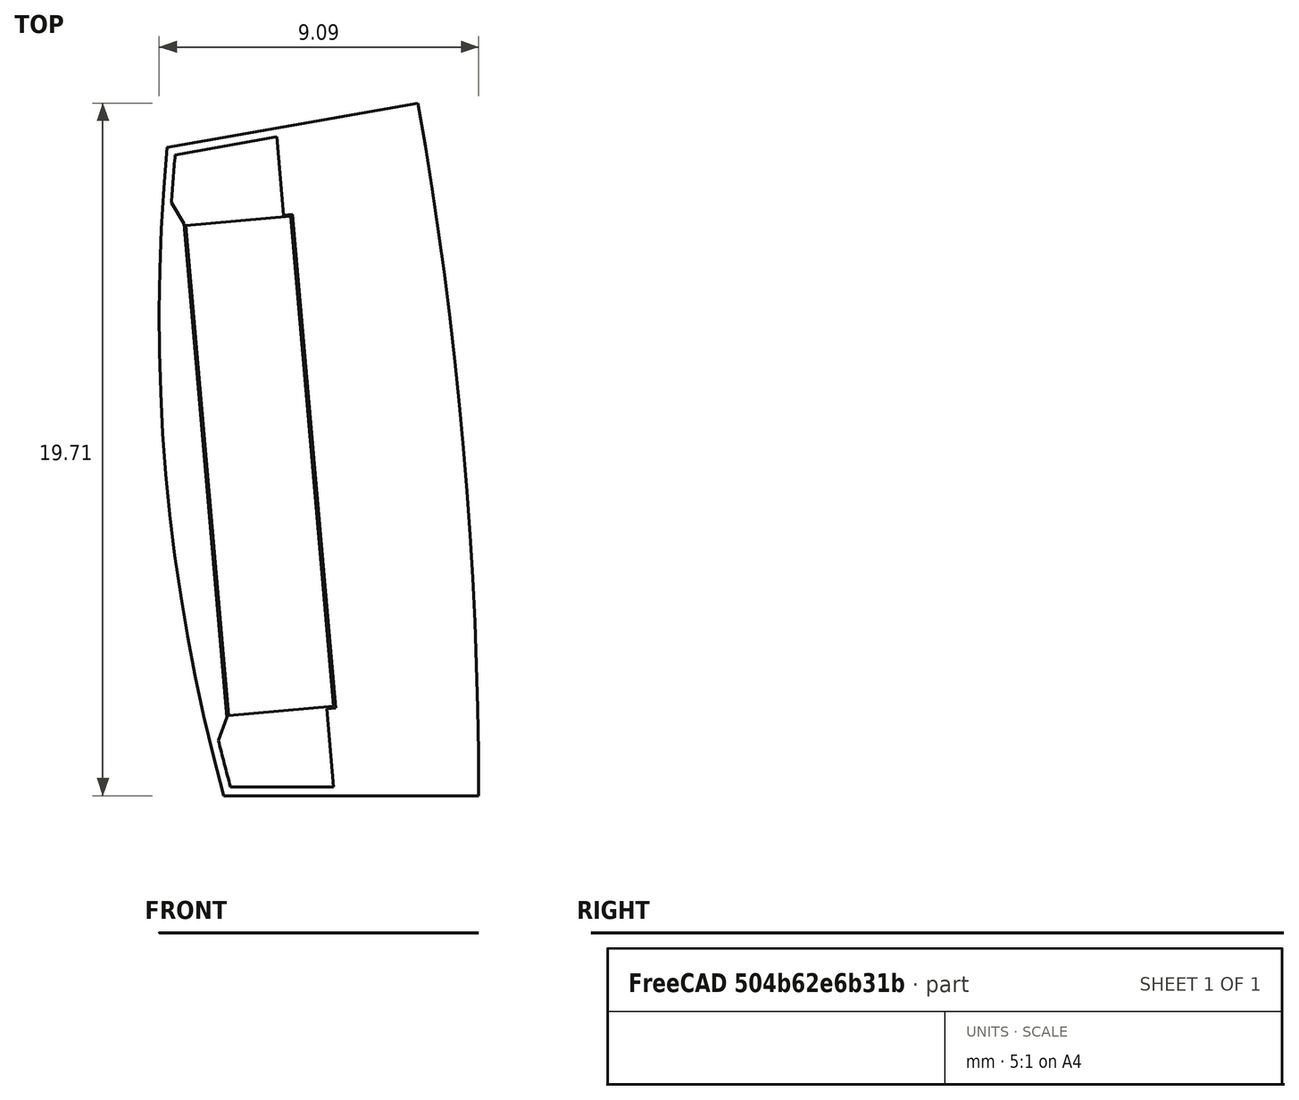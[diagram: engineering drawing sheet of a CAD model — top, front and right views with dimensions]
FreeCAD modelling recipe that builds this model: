
FCSTD DOCUMENT  (FreeCAD 0.18R4 (GitTag))
Label: RotorORBlockPocket
License: All rights reserved
LicenseURL: http://en.wikipedia.org/wiki/All_rights_reserved
objects: Sketcher::SketchObject×6, Surface::Filling×3, PartDesign::Body×2, Spreadsheet::Sheet×1, Part::Cut×1
note: 12 computed .brp shape members not serialized (recipe doc carries the construction recipe); baked Part::Feature solids carry a one-line shape summary decoded from their .brp

FEATURE [Spreadsheet::Sheet] Spreadsheet  label="Variables"
  cells = A2=poleNumber; B2(poleNumber)=36; C2=ok; A3=outerDiameter; B3(outerDiameter)=227; C3=ok; D3=Calc Value; A4=innerDiameter; B4(innerDiameter)=210; C4=ok; D4=Input Value; A5=stackLength; B5(stackLength)=20; C5=ok; D5=UsedParameter; A6=stackingFactor; B6(stackingFactor)=0.95; A7=embrace; B7(embrace)=80; A8=contourRatio; B8(contourRatio)=90; A9=magnetAirgap; B9(magnetAirgap)=0.05; C9=ok; A10=poleSeparation; B10(poleSeparation)=2; A11=magnetWidth; B11(magnetWidth)=14; C11=ok; A12=magnetHeight; B12(magnetHeight)=3; C12=ok; A13=rib; B13(rib)=0.5; C13=ok; A14=bridgeCurved; B14(bridgeCurved)=0.25; C14=ok; A15=cutTop; B15(cutTop)=0.2; A16=cutBottom; B16(cutBottom)=0.25; C16=ok; A17=segmentAngle; B17(segmentAngle)==360 / poleNumber; A18=movePocketInwards; B18(movePocketInwards)=0.3; C18=ok; A19=cuttingThickness; B19(cuttingThickness)=0.01; A20=magnetLength; B20(magnetLength)=20; A21=cut; B21(cut)=0.2; A22=ribShaft; B22(ribShaft)=0.5; A23=magnetEmbrace; B23(magnetEmbrace)=70; A24=magnetContourRatio; B24(magnetContourRatio)=95; A25=axialMisalignment; B25(axialMisalignment)=0.5; C25=ok; A26=magnetContactRatio; B26(magnetContactRatio)=83; C26=ok
FEATURE [Sketcher::SketchObject] Sketch003  label="RotorSketch"
  MapMode = 5
  Support = -> [XY_Plane]
  expr: Constraints[84] = Variables.magnetHeight + Variables.magnetAirgap * 2
  expr: Constraints[80] = Variables.movePocketInwards
  expr: Constraints[14] = Variables.innerDiameter / 2
  expr: Constraints[81] = Variables.magnetWidth + Variables.magnetAirgap * 2
  expr: Constraints[28] = Variables.segmentAngle * Variables.magnetContactRatio / 100
  expr: Constraints[48] = Variables.rib / 2
  expr: Constraints[86] = Variables.magnetHeight + Variables.magnetAirgap * 2 - Variables.cutBottom
  expr: Constraints[37] = Variables.bridgeCurved
  expr: Constraints[33] = (Variables.outerDiameter - Variables.innerDiameter) / 2 * (1 - Variables.contourRatio / 100)
  expr: Constraints[15] = Variables.outerDiameter / 2
  expr: Constraints[18] = Variables.segmentAngle / 2
  expr: Constraints[0] = Variables.segmentAngle
  expr: Constraints[40] = Variables.bridgeCurved
  sketch-geometry (38):
    g0: LineSegment [constr] StartX=105 StartY=0 StartZ=0 EndX=113.5 EndY=0 EndZ=0
    g1: LineSegment [constr] StartX=103.405 StartY=18.2331 StartZ=0 EndX=111.776 EndY=19.7091 EndZ=0
    g2: LineSegment [constr] StartX=0 StartY=0 StartZ=0 EndX=105 EndY=0 EndZ=0
    g3: LineSegment [constr] StartX=0 StartY=0 StartZ=0 EndX=103.405 EndY=18.2331 EndZ=0
    g4: ArcOfCircle CenterX=0 CenterY=0 CenterZ=0 NormalX=0 NormalY=0 NormalZ=1 AngleXU=0 Radius=113.5 StartAngle=0 EndAngle=0.174533
    g5: ArcOfCircle [constr] CenterX=0 CenterY=0 CenterZ=0 NormalX=0 NormalY=0 NormalZ=1 AngleXU=0 Radius=105 StartAngle=0 EndAngle=0.174533
    g6: LineSegment [constr] StartX=0 StartY=0 StartZ=0 EndX=113.068 EndY=9.89218 EndZ=0
    g7: LineSegment [constr] StartX=103.8 StartY=18.3027 StartZ=0 EndX=105.401 EndY=0 EndZ=0
    g8: LineSegment [constr] StartX=104.759 StartY=16.8734 StartZ=0 EndX=106.097 EndY=1.5741 EndZ=0
    g9: LineSegment [constr] StartX=0 StartY=0 StartZ=0 EndX=104.759 EndY=16.8734 EndZ=0
    g10: LineSegment [constr] StartX=0 StartY=0 StartZ=0 EndX=106.097 EndY=1.5741 EndZ=0
    g11: ArcOfCircle CenterX=155.466 CenterY=13.6015 CenterZ=0 NormalX=0 NormalY=0 NormalZ=1 AngleXU=0 Radius=51.0601 StartAngle=3.04649 EndAngle=3.41123
    g12: ArcOfCircle [constr] CenterX=155.715 CenterY=13.6233 CenterZ=0 NormalX=0 NormalY=0 NormalZ=1 AngleXU=0 Radius=51.0601 StartAngle=3.04604 EndAngle=3.41167
    g13: LineSegment [constr] StartX=104.6 StartY=9.15135 StartZ=0 EndX=104.849 EndY=9.17314 EndZ=0
    g14: LineSegment [constr] StartX=104.864 StartY=18.2365 StartZ=0 EndX=111.819 EndY=19.4628 EndZ=0
    g15: LineSegment [constr] StartX=111.819 StartY=19.4628 StartZ=0 EndX=111.775 EndY=19.709 EndZ=0
    g16: LineSegment [constr] StartX=113.5 StartY=0.25 StartZ=0 EndX=106.438 EndY=0.25 EndZ=0
    g17: LineSegment [constr] StartX=113.5 StartY=0.25 StartZ=0 EndX=113.5 EndY=0 EndZ=0
    g18: LineSegment [constr] StartX=104.864 StartY=18.2365 StartZ=0 EndX=106.438 EndY=0.25 EndZ=0
    g19: LineSegment StartX=104.637 StartY=18.4503 StartZ=0 EndX=111.776 EndY=19.7091 EndZ=0
    g20: LineSegment [constr] StartX=106.251 StartY=0 StartZ=0 EndX=113.5 EndY=0 EndZ=0
    g21: ArcOfCircle [constr] CenterX=155.715 CenterY=13.6233 CenterZ=0 NormalX=0 NormalY=0 NormalZ=1 AngleXU=0 Radius=51.0601 StartAngle=3.05112 EndAngle=3.0779
    g22: ArcOfCircle [constr] CenterX=155.715 CenterY=13.6233 CenterZ=0 NormalX=0 NormalY=0 NormalZ=1 AngleXU=0 Radius=51.0601 StartAngle=3.37982 EndAngle=3.4066
    g23: LineSegment [constr] StartX=104.759 StartY=16.8734 StartZ=0 EndX=104.508 EndY=18.4276 EndZ=0
    g24: LineSegment [constr] StartX=104.759 StartY=16.8734 StartZ=0 EndX=105.112 EndY=16.2731 EndZ=0
    g25: LineSegment [constr] StartX=105.112 StartY=16.2731 StartZ=0 EndX=106.341 EndY=2.22673 EndZ=0
    g26: LineSegment [constr] StartX=106.097 StartY=1.5741 StartZ=0 EndX=106.341 EndY=2.22673 EndZ=0
    g27: LineSegment [constr] StartX=104.759 StartY=16.8734 StartZ=0 EndX=105.058 EndY=16.8996 EndZ=0
    g28: LineSegment [constr] StartX=105.112 StartY=16.2731 StartZ=0 EndX=108.201 EndY=16.5433 EndZ=0
    g29: LineSegment [constr] StartX=105.112 StartY=16.2731 StartZ=0 EndX=107.952 EndY=16.5215 EndZ=0
    g30: LineSegment [constr] StartX=107.952 StartY=16.5215 StartZ=0 EndX=107.757 EndY=18.7466 EndZ=0
    g31: LineSegment [constr] StartX=107.952 StartY=16.5215 StartZ=0 EndX=108.201 EndY=16.5433 EndZ=0
    g32: LineSegment [constr] StartX=104.864 StartY=18.2365 StartZ=0 EndX=107.757 EndY=18.7466 EndZ=0
    g33: LineSegment [constr] StartX=109.43 StartY=2.49691 StartZ=0 EndX=109.18 EndY=2.47512 EndZ=0
    g34: LineSegment [constr] StartX=109.18 StartY=2.47512 StartZ=0 EndX=109.375 EndY=0.25 EndZ=0
    g35: LineSegment [constr] StartX=106.438 StartY=0.25 StartZ=0 EndX=109.375 EndY=0.25 EndZ=0
    g36: LineSegment [constr] StartX=109.43 StartY=2.49691 StartZ=0 EndX=108.201 EndY=16.5433 EndZ=0
    g37: LineSegment StartX=106.251 StartY=0 StartZ=0 EndX=113.5 EndY=0 EndZ=0
  constraints (105):
    c: Angle(g0,g1) = 0.174533
    c: Coincident(g2,g-1)
    c: Coincident(g2,g0)
    c: Coincident(g3,g2)
    c: Coincident(g3,g1)
    c: Parallel(g2,g0)
    c: Parallel(g3,g1)
    c: Coincident(g4,g-1)
    c: Coincident(g4,g0)
    c: Coincident(g4,g1)
    c: Coincident(g5,g4)
    c: Coincident(g5,g1)
    c: Coincident(g5,g0)
    c: Angle(g-1,g2) = 0
    c: Radius(g5) = 105
    c: Radius(g4) = 113.5
    c: Coincident(g6,g5)
    c: PointOnObject(g6,g4)
    c: Angle(g-1,g6) = 0.0872665
    c: PointOnObject(g7,g0)
    c: Tangent(g7,g5)
    c: Angle(g6,g7) = 1.5708
    c: PointOnObject(g7,g1)
    c: Symmetric(g8,g8,g6)
    c: Coincident(g9,g5)
    c: Coincident(g9,g8)
    c: Coincident(g10,g5)
    c: Coincident(g10,g8)
    c: Angle(g10,g9) = 0.144862
    c: PointOnObject(g11,g6)
    c: PointOnObject(g11,g1)
    c: PointOnObject(g11,g0)
    c: Tangent(g11,g7)
    c: Distance(g7,g11) = 0.85
    c: PointOnObject(g12,g6)
    c: PointOnObject(g12,g1)
    c: PointOnObject(g12,g0)
    c: Distance(g11,g12) = 0.25
    c: PointOnObject(g13,g11)
    c: PointOnObject(g13,g12)
    c: Distance(g13) = 0.25
    c: Parallel(g13,g6)
    c: PointOnObject(g13,g6)
    c: PointOnObject(g14,g12)
    c: PointOnObject(g14,g4)
    c: Coincident(g15,g14)
    c: PointOnObject(g15,g1)
    c: Angle(g15,g14) = 1.5708
    c: Distance(g15) = 0.25
    c: Angle(g1,g15) = 1.5708
    c: PointOnObject(g16,g4)
    c: Coincident(g17,g16)
    c: PointOnObject(g17,g0)
    c: Angle(g16,g17) = 1.5708
    c: Angle(g17,g0) = 1.5708
    c: Equal(g17,g15)
    c: Coincident(g18,g14)
    c: Coincident(g18,g16)
    c: Coincident(g19,g11)
    c: Coincident(g19,g1)
    c: Coincident(g20,g11)
    c: Coincident(g20,g17)
    c: Coincident(g21,g12)
    c: Coincident(g21,g8)
    c: Coincident(g21,g14)
    c: Coincident(g22,g21)
    c: Coincident(g22,g16)
    c: Coincident(g22,g8)
    c: Coincident(g23,g21)
    c: PointOnObject(g23,g1)
    c: Angle(g23,g9) = 1.5708
    c: Coincident(g24,g21)
    c: Coincident(g25,g24)
    c: Coincident(g26,g22)
    c: Coincident(g26,g25)
    c: Equal(g26,g24)
    c: Symmetric(g24,g25,g6)
    c: Coincident(g27,g21)
    c: PointOnObject(g27,g25)
    c: Angle(g27,g25) = 1.5708
    c: Distance(g27) = 0.3
    c: Distance(g25) = 14.1
    c: Coincident(g28,g24)
    c: Angle(g25,g28) = 1.5708
    c: Distance(g28) = 3.1
    c: Coincident(g29,g24)
    c: Distance(g29) = 2.85
    c: Angle(g25,g29) = 1.5708
    c: Coincident(g30,g29)
    c: PointOnObject(g30,g14)
    c: Coincident(g31,g30)
    c: Coincident(g31,g28)
    c: Coincident(g32,g21)
    c: Coincident(g32,g30)
    c: Parallel(g18,g30)
    c: Coincident(g34,g33)
    c: Symmetric(g31,g33,g6)
    c: Symmetric(g30,g33,g6)
    c: Symmetric(g30,g34,g6)
    c: Coincident(g35,g22)
    c: Coincident(g35,g34)
    c: Coincident(g36,g33)
    c: Coincident(g36,g31)
    c: Coincident(g37,g11)
    c: Coincident(g37,g4)
FEATURE [Sketcher::SketchObject] Sketch004  label="BoundingBox"
  MapMode = 5
  Support = -> [XY_Plane]
  expr: Constraints[8] = Variables.outerDiameter
  sketch-geometry (6):
    g0: LineSegment StartX=-113.5 StartY=-113.5 StartZ=0 EndX=113.5 EndY=-113.5 EndZ=0
    g1: LineSegment StartX=113.5 StartY=-113.5 StartZ=0 EndX=113.5 EndY=113.5 EndZ=0
    g2: LineSegment StartX=113.5 StartY=113.5 StartZ=0 EndX=-113.5 EndY=113.5 EndZ=0
    g3: LineSegment StartX=-113.5 StartY=113.5 StartZ=0 EndX=-113.5 EndY=-113.5 EndZ=0
    g4: LineSegment [constr] StartX=-113.5 StartY=-113.5 StartZ=0 EndX=113.5 EndY=113.5 EndZ=0
    g5: GeomPoint X=4.4e-15 Y=-1.8e-15 Z=0
  constraints (14):
    c: Coincident(g0,g1)
    c: Coincident(g1,g2)
    c: Coincident(g2,g3)
    c: Coincident(g3,g0)
    c: Horizontal(g0)
    c: Horizontal(g2)
    c: Vertical(g1)
    c: Vertical(g3)
    c: DistanceY(g1,g1) = 227
    c: Equal(g2,g1)
    c: Coincident(g4,g0)
    c: Coincident(g4,g1)
    c: Symmetric(g0,g1,g5)
    c: Coincident(g-1,g5)
FEATURE [Sketcher::SketchObject] Sketch005  label="RotorSideSketch"
  MapMode = 5
  Support = -> [XY_Plane001]
  expr: Constraints[22] = Variables.stackLength / 2 - Variables.axialMisalignment
  expr: Constraints[9] = Variables.outerDiameter / 2
  expr: Constraints[8] = Variables.innerDiameter / 2
  expr: Constraints[7] = Variables.stackLength
  sketch-geometry (8):
    g0: LineSegment StartX=-9.5 StartY=105 StartZ=0 EndX=10.5 EndY=105 EndZ=0
    g1: LineSegment StartX=10.5 StartY=105 StartZ=0 EndX=10.5 EndY=113.5 EndZ=0
    g2: LineSegment StartX=10.5 StartY=113.5 StartZ=0 EndX=-9.5 EndY=113.5 EndZ=0
    g3: LineSegment StartX=-9.5 StartY=113.5 StartZ=0 EndX=-9.5 EndY=105 EndZ=0
    g4: LineSegment StartX=-9.5 StartY=-105 StartZ=0 EndX=10.5 EndY=-105 EndZ=0
    g5: LineSegment StartX=10.5 StartY=-105 StartZ=0 EndX=10.5 EndY=-113.5 EndZ=0
    g6: LineSegment StartX=10.5 StartY=-113.5 StartZ=0 EndX=-9.5 EndY=-113.5 EndZ=0
    g7: LineSegment StartX=-9.5 StartY=-113.5 StartZ=0 EndX=-9.5 EndY=-105 EndZ=0
  constraints (23):
    c: Coincident(g0,g1)
    c: Coincident(g1,g2)
    c: Coincident(g2,g3)
    c: Coincident(g3,g0)
    c: Horizontal(g0)
    c: Vertical(g1)
    c: Vertical(g3)
    c: DistanceX(g2,g2) = 20
    c: DistanceY(g-1,g0) = 105
    c: DistanceY(g-1,g1) = 113.5
    c: Coincident(g4,g5)
    c: Coincident(g5,g6)
    c: Coincident(g6,g7)
    c: Coincident(g7,g4)
    c: Horizontal(g4)
    c: Vertical(g5)
    c: Vertical(g7)
    c: Equal(g4,g0)
    c: Equal(g7,g3)
    c: Horizontal(g2)
    c: Horizontal(g6)
    c: Symmetric(g4,g0,g-1)
    c: DistanceX(g0,g-1) = 9.5
FEATURE [Sketcher::SketchObject] Sketch006  label="MagnetSideSketch"
  MapMode = 5
  Support = -> [XY_Plane001]
  expr: Constraints[20] = Variables.stackLength / 2 - Variables.axialMisalignment
  expr: Constraints[17] = Variables.innerDiameter / 2
  expr: Constraints[14] = Variables.stackLength
  expr: Constraints[3] = Variables.magnetHeight
  sketch-geometry (8):
    g0: LineSegment StartX=-9.5 StartY=105 StartZ=0 EndX=10.5 EndY=105 EndZ=0
    g1: LineSegment StartX=10.5 StartY=105 StartZ=0 EndX=10.5 EndY=108 EndZ=0
    g2: LineSegment StartX=-9.5 StartY=108 StartZ=0 EndX=-9.5 EndY=105 EndZ=0
    g3: LineSegment StartX=-9.5 StartY=-105 StartZ=0 EndX=10.5 EndY=-105 EndZ=0
    g4: LineSegment StartX=10.5 StartY=-105 StartZ=0 EndX=10.5 EndY=-108 EndZ=0
    g5: LineSegment StartX=10.5 StartY=-108 StartZ=0 EndX=-9.5 EndY=-108 EndZ=0
    g6: LineSegment StartX=-9.5 StartY=-108 StartZ=0 EndX=-9.5 EndY=-105 EndZ=0
    g7: LineSegment StartX=-9.5 StartY=108 StartZ=0 EndX=10.5 EndY=108 EndZ=0
  constraints (23):
    c: Coincident(g0,g1)
    c: Coincident(g2,g0)
    c: Horizontal(g0)
    c: DistanceY(g1,g1) = 3
    c: Coincident(g3,g4)
    c: Coincident(g4,g5)
    c: Coincident(g5,g6)
    c: Coincident(g6,g3)
    c: Horizontal(g3)
    c: Vertical(g4)
    c: Vertical(g6)
    c: Equal(g6,g2)
    c: Coincident(g7,g2)
    c: Coincident(g7,g1)
    c: DistanceX(g7,g7) = 20
    c: Horizontal(g5)
    c: Equal(g6,g1)
    c: DistanceY(g-1,g0) = 105
    c: Symmetric(g0,g3,g-1)
    c: Equal(g5,g7)
    c: DistanceX(g0,g-1) = 9.5
    c: Angle(g0,g2) = 1.5708
    c: Angle(g1,g0) = 1.5708
FEATURE [PartDesign::Body] Body001  label="SideView"
  Group = -> [Sketch005,Sketch006]
  Origin = -> Origin001
FEATURE [Surface::Filling] Surface001  label="Pole_Surface"
  Anisotropy = false
  BoundaryEdges = -> [Sketch003]
  BoundaryOrder = [0,0,0,0]
  Degree = 3
  Iterations = 2
  MaximumDegree = 8
  MaximumSegments = 9
  PointsOnCurve = 15
  TolAngular = 0.01
  TolCurvature = 0.1
  Tolerance2d = 1e-05
  Tolerance3d = 0.0001
FEATURE [Sketcher::SketchObject] Sketch007  label="PocketSketch"
  MapMode = 5
  Support = -> [XY_Plane]
  expr: Constraints[84] = Variables.magnetHeight + Variables.magnetAirgap * 2
  expr: Constraints[80] = Variables.movePocketInwards
  expr: Constraints[14] = Variables.innerDiameter / 2
  expr: Constraints[81] = Variables.magnetWidth + Variables.magnetAirgap * 2
  expr: Constraints[28] = Variables.segmentAngle * Variables.magnetContactRatio / 100
  expr: Constraints[48] = Variables.rib / 2
  expr: Constraints[86] = Variables.magnetHeight + Variables.magnetAirgap * 2 - Variables.cutBottom
  expr: Constraints[37] = Variables.bridgeCurved
  expr: Constraints[33] = (Variables.outerDiameter - Variables.innerDiameter) / 2 * (1 - Variables.contourRatio / 100)
  expr: Constraints[15] = Variables.outerDiameter / 2
  expr: Constraints[18] = Variables.segmentAngle / 2
  expr: Constraints[0] = Variables.segmentAngle
  expr: Constraints[40] = Variables.bridgeCurved
  sketch-geometry (38):
    g0: LineSegment [constr] StartX=105 StartY=0 StartZ=0 EndX=113.5 EndY=0 EndZ=0
    g1: LineSegment [constr] StartX=103.405 StartY=18.2331 StartZ=0 EndX=111.776 EndY=19.7091 EndZ=0
    g2: LineSegment [constr] StartX=0 StartY=0 StartZ=0 EndX=105 EndY=0 EndZ=0
    g3: LineSegment [constr] StartX=0 StartY=0 StartZ=0 EndX=103.405 EndY=18.2331 EndZ=0
    g4: ArcOfCircle [constr] CenterX=0 CenterY=0 CenterZ=0 NormalX=0 NormalY=0 NormalZ=1 AngleXU=0 Radius=113.5 StartAngle=0 EndAngle=0.174533
    g5: ArcOfCircle [constr] CenterX=0 CenterY=0 CenterZ=0 NormalX=0 NormalY=0 NormalZ=1 AngleXU=0 Radius=105 StartAngle=0 EndAngle=0.174533
    g6: LineSegment [constr] StartX=0 StartY=0 StartZ=0 EndX=113.068 EndY=9.89218 EndZ=0
    g7: LineSegment [constr] StartX=103.8 StartY=18.3027 StartZ=0 EndX=105.401 EndY=0 EndZ=0
    g8: LineSegment [constr] StartX=104.759 StartY=16.8734 StartZ=0 EndX=106.097 EndY=1.5741 EndZ=0
    g9: LineSegment [constr] StartX=0 StartY=0 StartZ=0 EndX=104.759 EndY=16.8734 EndZ=0
    g10: LineSegment [constr] StartX=0 StartY=0 StartZ=0 EndX=106.097 EndY=1.5741 EndZ=0
    g11: ArcOfCircle [constr] CenterX=155.466 CenterY=13.6015 CenterZ=0 NormalX=0 NormalY=0 NormalZ=1 AngleXU=0 Radius=51.0601 StartAngle=3.04649 EndAngle=3.41123
    g12: ArcOfCircle [constr] CenterX=155.715 CenterY=13.6233 CenterZ=0 NormalX=0 NormalY=0 NormalZ=1 AngleXU=0 Radius=51.0601 StartAngle=3.04604 EndAngle=3.41167
    g13: LineSegment [constr] StartX=104.6 StartY=9.15135 StartZ=0 EndX=104.849 EndY=9.17314 EndZ=0
    g14: LineSegment [constr] StartX=104.864 StartY=18.2365 StartZ=0 EndX=111.819 EndY=19.4628 EndZ=0
    g15: LineSegment [constr] StartX=111.819 StartY=19.4628 StartZ=0 EndX=111.775 EndY=19.709 EndZ=0
    g16: LineSegment [constr] StartX=113.5 StartY=0.25 StartZ=0 EndX=106.438 EndY=0.25 EndZ=0
    g17: LineSegment [constr] StartX=113.5 StartY=0.25 StartZ=0 EndX=113.5 EndY=0 EndZ=0
    g18: LineSegment [constr] StartX=104.864 StartY=18.2365 StartZ=0 EndX=106.438 EndY=0.25 EndZ=0
    g19: LineSegment [constr] StartX=104.637 StartY=18.4503 StartZ=0 EndX=111.776 EndY=19.7091 EndZ=0
    g20: LineSegment [constr] StartX=106.251 StartY=0 StartZ=0 EndX=113.5 EndY=0 EndZ=0
    g21: ArcOfCircle CenterX=155.715 CenterY=13.6233 CenterZ=0 NormalX=0 NormalY=0 NormalZ=1 AngleXU=0 Radius=51.0601 StartAngle=3.05112 EndAngle=3.0779
    g22: ArcOfCircle CenterX=155.715 CenterY=13.6233 CenterZ=0 NormalX=0 NormalY=0 NormalZ=1 AngleXU=0 Radius=51.0601 StartAngle=3.37982 EndAngle=3.4066
    g23: LineSegment [constr] StartX=104.759 StartY=16.8734 StartZ=0 EndX=104.508 EndY=18.4276 EndZ=0
    g24: LineSegment StartX=104.759 StartY=16.8734 StartZ=0 EndX=105.112 EndY=16.2731 EndZ=0
    g25: LineSegment StartX=105.112 StartY=16.2731 StartZ=0 EndX=106.341 EndY=2.22673 EndZ=0
    g26: LineSegment StartX=106.097 StartY=1.5741 StartZ=0 EndX=106.341 EndY=2.22673 EndZ=0
    g27: LineSegment [constr] StartX=104.759 StartY=16.8734 StartZ=0 EndX=105.058 EndY=16.8996 EndZ=0
    g28: LineSegment [constr] StartX=105.112 StartY=16.2731 StartZ=0 EndX=108.201 EndY=16.5433 EndZ=0
    g29: LineSegment [constr] StartX=105.112 StartY=16.2731 StartZ=0 EndX=107.952 EndY=16.5215 EndZ=0
    g30: LineSegment StartX=107.952 StartY=16.5215 StartZ=0 EndX=107.757 EndY=18.7466 EndZ=0
    g31: LineSegment StartX=107.952 StartY=16.5215 StartZ=0 EndX=108.201 EndY=16.5433 EndZ=0
    g32: LineSegment StartX=104.864 StartY=18.2365 StartZ=0 EndX=107.757 EndY=18.7466 EndZ=0
    g33: LineSegment StartX=109.43 StartY=2.49691 StartZ=0 EndX=109.18 EndY=2.47512 EndZ=0
    g34: LineSegment StartX=109.18 StartY=2.47512 StartZ=0 EndX=109.375 EndY=0.25 EndZ=0
    g35: LineSegment StartX=106.438 StartY=0.25 StartZ=0 EndX=109.375 EndY=0.25 EndZ=0
    g36: LineSegment StartX=109.43 StartY=2.49691 StartZ=0 EndX=108.201 EndY=16.5433 EndZ=0
    g37: LineSegment [constr] StartX=106.251 StartY=0 StartZ=0 EndX=113.5 EndY=0 EndZ=0
  constraints (105):
    c: Angle(g0,g1) = 0.174533
    c: Coincident(g2,g-1)
    c: Coincident(g2,g0)
    c: Coincident(g3,g2)
    c: Coincident(g3,g1)
    c: Parallel(g2,g0)
    c: Parallel(g3,g1)
    c: Coincident(g4,g-1)
    c: Coincident(g4,g0)
    c: Coincident(g4,g1)
    c: Coincident(g5,g4)
    c: Coincident(g5,g1)
    c: Coincident(g5,g0)
    c: Angle(g-1,g2) = 0
    c: Radius(g5) = 105
    c: Radius(g4) = 113.5
    c: Coincident(g6,g5)
    c: PointOnObject(g6,g4)
    c: Angle(g-1,g6) = 0.0872665
    c: PointOnObject(g7,g0)
    c: Tangent(g7,g5)
    c: Angle(g6,g7) = 1.5708
    c: PointOnObject(g7,g1)
    c: Symmetric(g8,g8,g6)
    c: Coincident(g9,g5)
    c: Coincident(g9,g8)
    c: Coincident(g10,g5)
    c: Coincident(g10,g8)
    c: Angle(g10,g9) = 0.144862
    c: PointOnObject(g11,g6)
    c: PointOnObject(g11,g1)
    c: PointOnObject(g11,g0)
    c: Tangent(g11,g7)
    c: Distance(g7,g11) = 0.85
    c: PointOnObject(g12,g6)
    c: PointOnObject(g12,g1)
    c: PointOnObject(g12,g0)
    c: Distance(g11,g12) = 0.25
    c: PointOnObject(g13,g11)
    c: PointOnObject(g13,g12)
    c: Distance(g13) = 0.25
    c: Parallel(g13,g6)
    c: PointOnObject(g13,g6)
    c: PointOnObject(g14,g12)
    c: PointOnObject(g14,g4)
    c: Coincident(g15,g14)
    c: PointOnObject(g15,g1)
    c: Angle(g15,g14) = 1.5708
    c: Distance(g15) = 0.25
    c: Angle(g1,g15) = 1.5708
    c: PointOnObject(g16,g4)
    c: Coincident(g17,g16)
    c: PointOnObject(g17,g0)
    c: Angle(g16,g17) = 1.5708
    c: Angle(g17,g0) = 1.5708
    c: Equal(g17,g15)
    c: Coincident(g18,g14)
    c: Coincident(g18,g16)
    c: Coincident(g19,g11)
    c: Coincident(g19,g1)
    c: Coincident(g20,g11)
    c: Coincident(g20,g17)
    c: Coincident(g21,g12)
    c: Coincident(g21,g8)
    c: Coincident(g21,g14)
    c: Coincident(g22,g21)
    c: Coincident(g22,g16)
    c: Coincident(g22,g8)
    c: Coincident(g23,g21)
    c: PointOnObject(g23,g1)
    c: Angle(g23,g9) = 1.5708
    c: Coincident(g24,g21)
    c: Coincident(g25,g24)
    c: Coincident(g26,g22)
    c: Coincident(g26,g25)
    c: Equal(g26,g24)
    c: Symmetric(g24,g25,g6)
    c: Coincident(g27,g21)
    c: PointOnObject(g27,g25)
    c: Angle(g27,g25) = 1.5708
    c: Distance(g27) = 0.3
    c: Distance(g25) = 14.1
    c: Coincident(g28,g24)
    c: Angle(g25,g28) = 1.5708
    c: Distance(g28) = 3.1
    c: Coincident(g29,g24)
    c: Distance(g29) = 2.85
    c: Angle(g25,g29) = 1.5708
    c: Coincident(g30,g29)
    c: PointOnObject(g30,g14)
    c: Coincident(g31,g30)
    c: Coincident(g31,g28)
    c: Coincident(g32,g21)
    c: Coincident(g32,g30)
    c: Parallel(g18,g30)
    c: Coincident(g34,g33)
    c: Symmetric(g31,g33,g6)
    c: Symmetric(g30,g33,g6)
    c: Symmetric(g30,g34,g6)
    c: Coincident(g35,g22)
    c: Coincident(g35,g34)
    c: Coincident(g36,g33)
    c: Coincident(g36,g31)
    c: Coincident(g37,g11)
    c: Coincident(g37,g4)
FEATURE [Sketcher::SketchObject] Sketch  label="MagnetSketch"
  ExternalGeometry = -> [Sketch007]
  MapMode = 5
  Support = -> [XY_Plane]
  expr: Constraints[13] = Variables.magnetWidth
  expr: Constraints[12] = Variables.magnetHeight
  expr: Constraints[11] = Variables.magnetAirgap
  sketch-geometry (6):
    g0: LineSegment [constr] StartX=108.151 StartY=16.5389 StartZ=0 EndX=108.155 EndY=16.4891 EndZ=0
    g1: LineSegment [constr] StartX=108.155 StartY=16.4891 StartZ=0 EndX=108.205 EndY=16.4934 EndZ=0
    g2: LineSegment StartX=108.155 StartY=16.4891 StartZ=0 EndX=105.167 EndY=16.2276 EndZ=0
    g3: LineSegment StartX=105.167 StartY=16.2276 StartZ=0 EndX=106.387 EndY=2.2809 EndZ=0
    g4: LineSegment StartX=106.387 StartY=2.2809 StartZ=0 EndX=109.375 EndY=2.54236 EndZ=0
    g5: LineSegment StartX=108.155 StartY=16.4891 StartZ=0 EndX=109.375 EndY=2.54236 EndZ=0
  constraints (18):
    c: Coincident(g0,g1)
    c: Coincident(g4,g5)
    c: Angle(g5,g4) = 1.5708
    c: Coincident(g3,g4)
    c: Angle(g4,g3) = 1.5708
    c: Coincident(g3,g2)
    c: Angle(g3,g2) = 1.5708
    c: Coincident(g5,g0)
    c: Coincident(g2,g5)
    c: Equal(g0,g1)
    c: Angle(g0,g2) = 1.5708
    c: Distance(g1) = 0.05
    c: Distance(g2) = 3
    c: Distance(g3) = 14
    c: PointOnObject(g0,g-14)
    c: PointOnObject(g1,g-3)
    c: Angle(g1,g-3) = 1.5708
    c: Angle(g-14,g0) = 1.5708
FEATURE [PartDesign::Body] Body  label="TopView"
  Group = -> [Sketch003,Sketch004,Sketch,Sketch007]
  Origin = -> Origin
FEATURE [Surface::Filling] Surface  label="Magnet_Surface"
  Anisotropy = false
  BoundaryEdges = -> [Sketch]
  BoundaryOrder = [0,0,0,0]
  Degree = 3
  Iterations = 2
  MaximumDegree = 8
  MaximumSegments = 9
  PointsOnCurve = 15
  TolAngular = 0.01
  TolCurvature = 0.1
  Tolerance2d = 1e-05
  Tolerance3d = 0.0001
FEATURE [Surface::Filling] Surface002  label="Pocket_Surface"
  Anisotropy = false
  BoundaryEdges = -> [Sketch007]
  BoundaryOrder = [0,0,0,0,0,0,0,0,0,0,0,0]
  Degree = 3
  Iterations = 2
  MaximumDegree = 8
  MaximumSegments = 9
  PointsOnCurve = 15
  TolAngular = 0.01
  TolCurvature = 0.1
  Tolerance2d = 1e-05
  Tolerance3d = 0.0001
FEATURE [Part::Cut] Cut  label="Rotor_Surface"
  Base = -> Surface001
  Tool = -> Surface002
